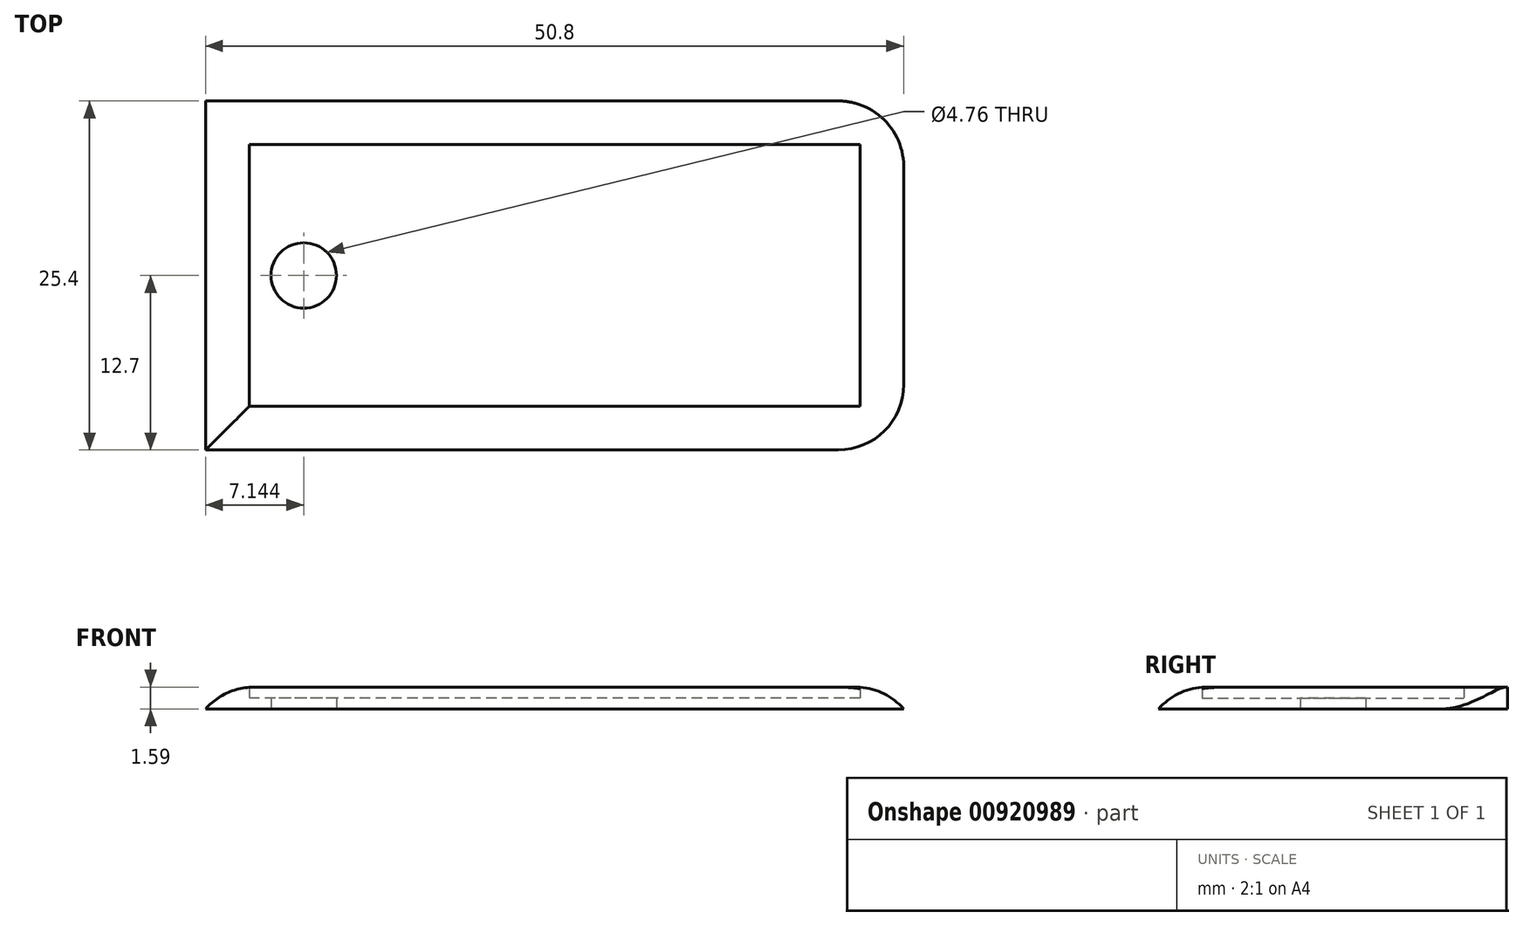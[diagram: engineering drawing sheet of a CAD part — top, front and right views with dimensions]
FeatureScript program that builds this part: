
annotation { "Feature Type Name" : "Feature", "Feature Type Description" : "" }
export const myFeature = defineFeature(function(context is Context, id is Id, definition is map)
    precondition{}
    {
        {
            var Q0;
            Q0=qCreatedBy(makeId("Top.planeOp"),FACE);
            var sketch = newSketch(context, id + "F0", { "sketchPlane" : qUnion([Q0])});
            skLineSegment(sketch, "E0.bottom", {"start": v(0, 25.4) * mm, "end": v(50.8, 25.4) * mm});
            skLineSegment(sketch, "E0.top", {"start": v(0, 0) * mm, "end": v(50.8, 0) * mm});
            skLineSegment(sketch, "E0.left", {"start": v(0, 25.4) * mm, "end": v(0, 0) * mm});
            skLineSegment(sketch, "E0.right", {"start": v(50.8, 25.4) * mm, "end": v(50.8, 0) * mm});
            skCircle(sketch, "E1", {"center": v(7.14, 12.7) * mm, "radius": 2.38 * mm});
            skPoint(sketch, "E2", {"position": v(0, 12.7) * mm});
            skLineSegment(sketch, "E3.bottom", {"start": v(3.18, 22.22) * mm, "end": v(47.63, 22.22) * mm});
            skLineSegment(sketch, "E3.top", {"start": v(3.18, 3.17) * mm, "end": v(47.63, 3.17) * mm});
            skLineSegment(sketch, "E3.left", {"start": v(3.18, 22.22) * mm, "end": v(3.18, 3.17) * mm});
            skLineSegment(sketch, "E3.right", {"start": v(47.63, 22.22) * mm, "end": v(47.63, 3.17) * mm});
            skSolve(sketch);
        }
        {
            var Q0;
            Q0=makeQuery(id+"F0.imprint","IMPRINT",FACE,{"disambiguationData":[TD([[makeQuery(id+"F0.imprint","IMPRINT",EDGE,{"derivedFrom":sQuery(id+"F0.wireOp",EDGE,"E1")}),-1.0]])]});
            var Q1;
            Q1=makeQuery(id+"F0.imprint","IMPRINT",FACE,{"disambiguationData":[TD([[makeQuery(id+"F0.imprint","IMPRINT",EDGE,{"derivedFrom":sQuery(id+"F0.wireOp",EDGE,"E0.bottom")}),-1.0]])]});
            extrude(context, id + "F1", {"entities" : qUnion([Q0, Q1]), "depth" : 0.8 * mm, "offsetDistance" : 25.4 * mm});
        }
        {
            var Q0;
            Q0=qSketchRegion(id+"F0",true);
            extrude(context, id + "F2", {"entities" : qUnion([Q0]), "operationType" : NewBodyOperationType.ADD, "depth" : 1.59 * mm, "offsetDistance" : 25.4 * mm});
        }
        {
            var Q0;
            Q0=makeQuery(id+"F2.opExtrude","SWEPT_EDGE",EDGE,{"disambiguationData":[OSD([sQuery(id+"F0.wireOp",EDGE,"E0.top"),sQuery(id+"F0.wireOp",EDGE,"E0.right")])]});
            fillet(context, id + "F3", {"entities" : qUnion([Q0]), "radius" : 4.76 * mm, "tangentPropagation" : true, "allowEdgeOverflow" : false});
        }
        {
            var Q0;
            Q0=makeQuery(id+"F2.opExtrude","SWEPT_EDGE",EDGE,{"disambiguationData":[OSD([sQuery(id+"F0.wireOp",EDGE,"E0.bottom"),sQuery(id+"F0.wireOp",EDGE,"E0.right")])]});
            var Q1;
            Q1=makeQuery(id+"F2.opExtrude","CAP_EDGE",EDGE,{"disambiguationData":[OSD([sQuery(id+"F0.wireOp",EDGE,"E0.top")])],"isStart":false});
            var Q2;
            Q2=makeQuery(id+"F2.opExtrude","CAP_EDGE",EDGE,{"disambiguationData":[OSD([sQuery(id+"F0.wireOp",EDGE,"E0.left")])],"isStart":true});
            fillet(context, id + "F4", {"entities" : qUnion([Q0, Q1, Q2]), "radius" : 4.76 * mm, "tangentPropagation" : true, "allowEdgeOverflow" : false});
        }
        {
            var Q0;
            {var subQ0=sQuery(id+"F0.wireOp",EDGE,"E0.left");Q0=makeQuery(id+"F4.opFillet","BLEND_EDGE",EDGE,{"blendedFrom":[makeQuery(id+"F2.opExtrude","CAP_EDGE",EDGE,{"disambiguationData":[OSD([sQuery(id+"F0.wireOp",EDGE,"E0.top")])],"isStart":false}),makeQuery(id+"F2.boolean.opBoolean","MERGE",FACE,{"derivedFrom":[makeQuery(id+"F1.opExtrude","SWEPT_FACE",FACE,{"disambiguationData":[OSD([subQ0])]}),makeQuery(id+"F2.opExtrude","SWEPT_FACE",FACE,{"disambiguationData":[OSD([subQ0])]})]})],"blendedInto":[makeQuery(id+"F2.boolean.opBoolean","MERGE",FACE,{"derivedFrom":[makeQuery(id+"F1.opExtrude","SWEPT_FACE",FACE,{"disambiguationData":[OSD([subQ0])]}),makeQuery(id+"F2.opExtrude","SWEPT_FACE",FACE,{"disambiguationData":[OSD([subQ0])]})]})]});}
            fillet(context, id + "F5", {"entities" : qUnion([Q0]), "radius" : 4.76 * mm, "tangentPropagation" : true, "allowEdgeOverflow" : false});
        }
    });
